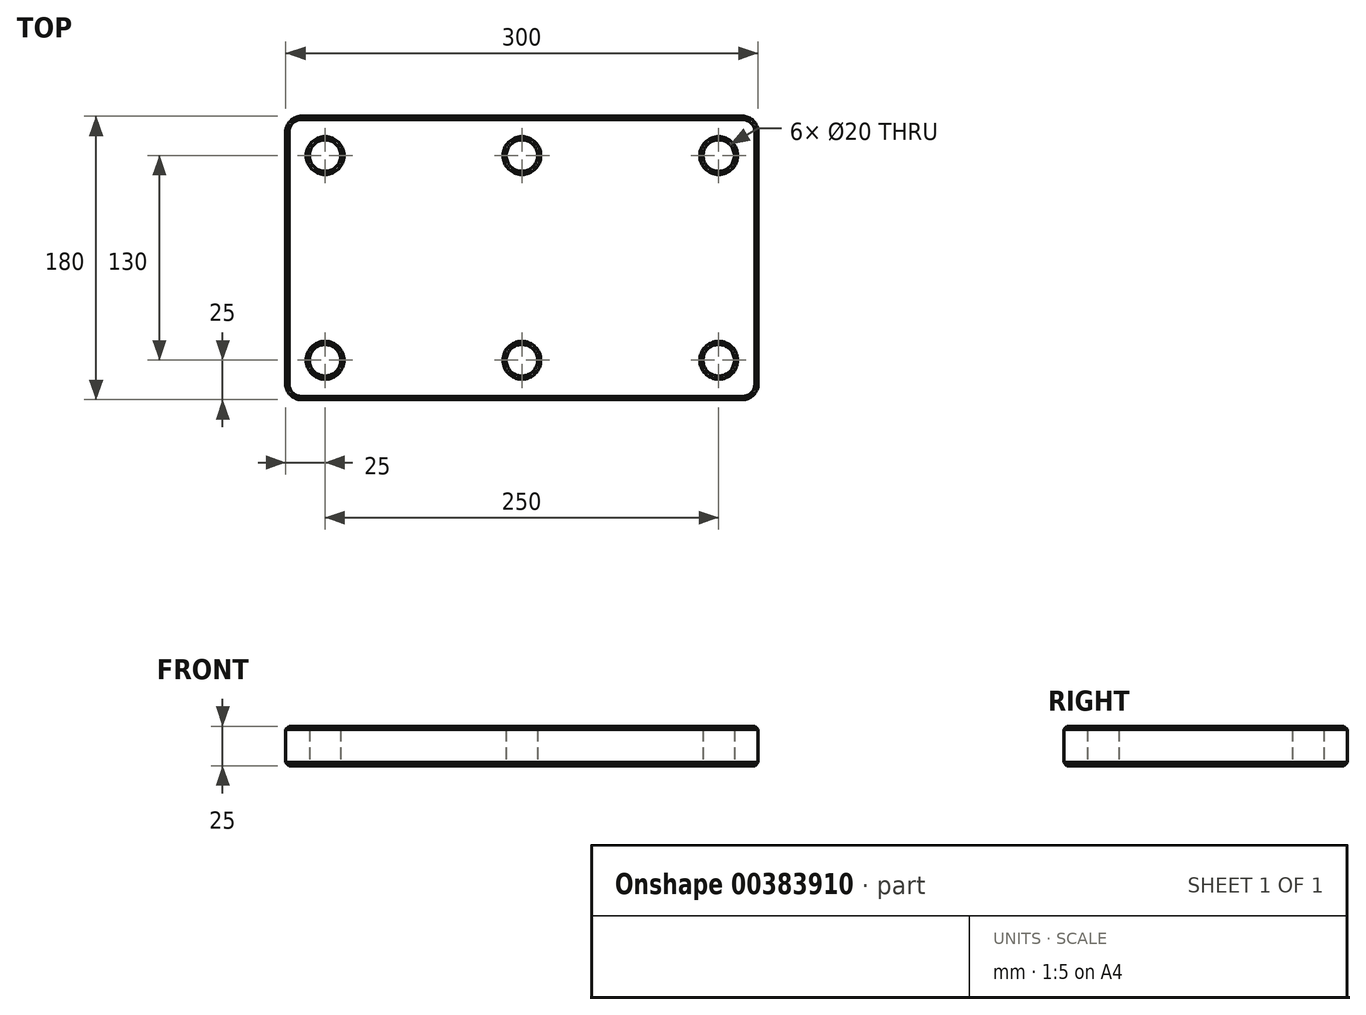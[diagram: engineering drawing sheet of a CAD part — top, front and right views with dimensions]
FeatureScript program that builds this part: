
annotation { "Feature Type Name" : "Feature", "Feature Type Description" : "" }
export const myFeature = defineFeature(function(context is Context, id is Id, definition is map)
    precondition{}
    {
        {
            var Q0;
            Q0=qCreatedBy(makeId("Top.planeOp"),FACE);
            var sketch = newSketch(context, id + "F0", { "sketchPlane" : qUnion([Q0])});
            skLineSegment(sketch, "E0.bottom", {"start": v(0, 0) * mm, "end": v(300, 0) * mm});
            skLineSegment(sketch, "E0.top", {"start": v(0, 180) * mm, "end": v(300, 180) * mm});
            skLineSegment(sketch, "E0.left", {"start": v(0, 0) * mm, "end": v(0, 180) * mm});
            skLineSegment(sketch, "E0.right", {"start": v(300, 0) * mm, "end": v(300, 180) * mm});
            skLineSegment(sketch, "E1", {"start": v(0, 155) * mm, "end": v(300, 155) * mm, "construction": true});
            skLineSegment(sketch, "E2", {"start": v(0, 25) * mm, "end": v(300, 25) * mm, "construction": true});
            skCircle(sketch, "E3", {"center": v(25, 155) * mm, "radius": 10 * mm});
            skCircle(sketch, "E4", {"center": v(150, 155) * mm, "radius": 10 * mm});
            skCircle(sketch, "E5", {"center": v(275, 155) * mm, "radius": 10 * mm});
            skCircle(sketch, "E6", {"center": v(25, 25) * mm, "radius": 10 * mm});
            skCircle(sketch, "E7", {"center": v(275, 25) * mm, "radius": 10 * mm});
            skCircle(sketch, "E8", {"center": v(150, 25) * mm, "radius": 10 * mm});
            skSolve(sketch);
        }
        {
            var Q0;
            Q0 = qSketchRegion(id + "F0", true);
            extrude(context, id + "F1", {"entities" : qUnion([Q0]), "depth" : 25 * mm});
        }
        {
            var Q0;
            Q0=makeQuery(id+"F1.opExtrude","CAP_EDGE",EDGE,{"disambiguationData":[OSD([sQuery(id+"F0.wireOp",EDGE,"E3")])],"isStart":false});
            var Q1;
            Q1=makeQuery(id+"F1.opExtrude","CAP_EDGE",EDGE,{"disambiguationData":[OSD([sQuery(id+"F0.wireOp",EDGE,"E6")])],"isStart":false});
            var Q2;
            Q2=makeQuery(id+"F1.opExtrude","CAP_EDGE",EDGE,{"disambiguationData":[OSD([sQuery(id+"F0.wireOp",EDGE,"E8")])],"isStart":false});
            var Q3;
            Q3=makeQuery(id+"F1.opExtrude","CAP_EDGE",EDGE,{"disambiguationData":[OSD([sQuery(id+"F0.wireOp",EDGE,"E4")])],"isStart":false});
            var Q4;
            Q4=makeQuery(id+"F1.opExtrude","CAP_EDGE",EDGE,{"disambiguationData":[OSD([sQuery(id+"F0.wireOp",EDGE,"E5")])],"isStart":false});
            var Q5;
            Q5=makeQuery(id+"F1.opExtrude","CAP_EDGE",EDGE,{"disambiguationData":[OSD([sQuery(id+"F0.wireOp",EDGE,"E7")])],"isStart":false});
            var Q6;
            Q6=makeQuery(id+"F1.opExtrude","CAP_EDGE",EDGE,{"disambiguationData":[OSD([sQuery(id+"F0.wireOp",EDGE,"E7")])],"isStart":true});
            var Q7;
            Q7=makeQuery(id+"F1.opExtrude","CAP_EDGE",EDGE,{"disambiguationData":[OSD([sQuery(id+"F0.wireOp",EDGE,"E5")])],"isStart":true});
            var Q8;
            Q8=makeQuery(id+"F1.opExtrude","CAP_EDGE",EDGE,{"disambiguationData":[OSD([sQuery(id+"F0.wireOp",EDGE,"E4")])],"isStart":true});
            var Q9;
            Q9=makeQuery(id+"F1.opExtrude","CAP_EDGE",EDGE,{"disambiguationData":[OSD([sQuery(id+"F0.wireOp",EDGE,"E8")])],"isStart":true});
            var Q10;
            Q10=makeQuery(id+"F1.opExtrude","CAP_EDGE",EDGE,{"disambiguationData":[OSD([sQuery(id+"F0.wireOp",EDGE,"E6")])],"isStart":true});
            var Q11;
            Q11=makeQuery(id+"F1.opExtrude","CAP_EDGE",EDGE,{"disambiguationData":[OSD([sQuery(id+"F0.wireOp",EDGE,"E3")])],"isStart":true});
            chamfer(context, id + "F2", {"entities" : qUnion([Q0, Q1, Q2, Q3, Q4, Q5, Q6, Q7, Q8, Q9, Q10, Q11]), "chamferType" : ChamferType.OFFSET_ANGLE, "width" : 2 * mm, "oppositeDirection" : false, "angle" : 45 * degree, "tangentPropagation" : true});
        }
        {
            var Q0;
            Q0=makeQuery(id+"F1.opExtrude","SWEPT_EDGE",EDGE,{"disambiguationData":[OSD([sQuery(id+"F0.wireOp",EDGE,"E0.bottom"),sQuery(id+"F0.wireOp",EDGE,"E0.left")])]});
            var Q1;
            Q1=makeQuery(id+"F1.opExtrude","SWEPT_EDGE",EDGE,{"disambiguationData":[OSD([sQuery(id+"F0.wireOp",EDGE,"E0.top"),sQuery(id+"F0.wireOp",EDGE,"E0.left")])]});
            var Q2;
            Q2=makeQuery(id+"F1.opExtrude","SWEPT_EDGE",EDGE,{"disambiguationData":[OSD([sQuery(id+"F0.wireOp",EDGE,"E0.bottom"),sQuery(id+"F0.wireOp",EDGE,"E0.right")])]});
            var Q3;
            Q3=makeQuery(id+"F1.opExtrude","SWEPT_EDGE",EDGE,{"disambiguationData":[OSD([sQuery(id+"F0.wireOp",EDGE,"E0.top"),sQuery(id+"F0.wireOp",EDGE,"E0.right")])]});
            fillet(context, id + "F3", {"entities" : qUnion([Q0, Q1, Q2, Q3]), "radius" : 10 * mm, "tangentPropagation" : true, "allowEdgeOverflow" : false});
        }
        {
            var Q0;
            Q0=makeQuery(id+"F1.opExtrude","CAP_EDGE",EDGE,{"disambiguationData":[OSD([sQuery(id+"F0.wireOp",EDGE,"E0.top")])],"isStart":false});
            var Q1;
            Q1=makeQuery(id+"F1.opExtrude","CAP_EDGE",EDGE,{"disambiguationData":[OSD([sQuery(id+"F0.wireOp",EDGE,"E0.bottom")])],"isStart":true});
            chamfer(context, id + "F4", {"entities" : qUnion([Q0, Q1]), "chamferType" : ChamferType.OFFSET_ANGLE, "width" : 2 * mm, "oppositeDirection" : false, "angle" : 45 * degree, "tangentPropagation" : true});
        }
    });
